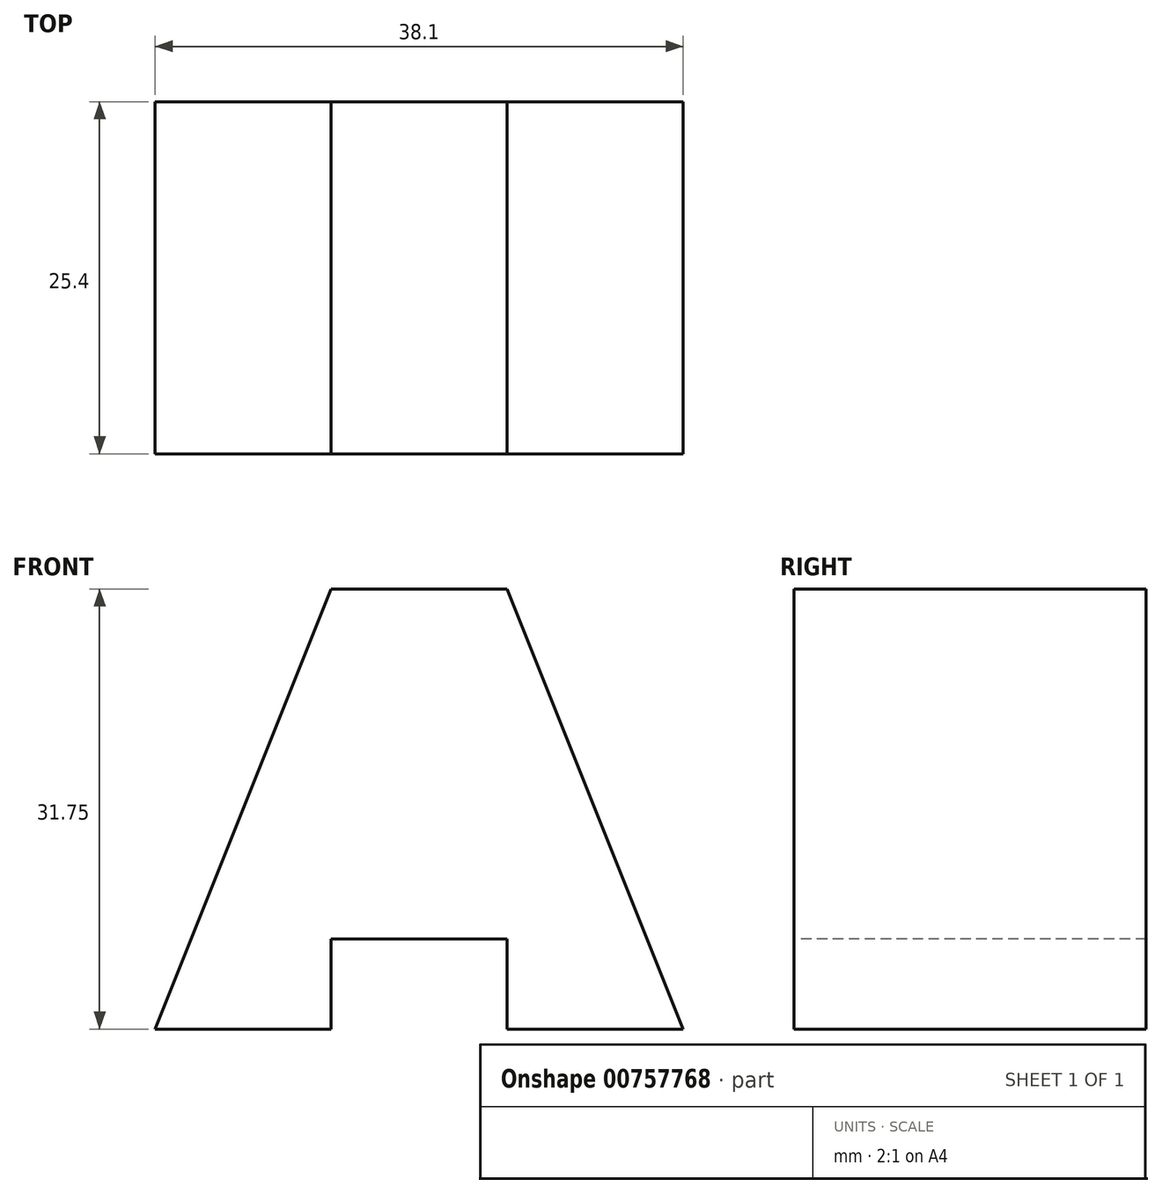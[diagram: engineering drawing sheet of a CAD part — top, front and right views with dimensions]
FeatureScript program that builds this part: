
annotation { "Feature Type Name" : "Feature", "Feature Type Description" : "" }
export const myFeature = defineFeature(function(context is Context, id is Id, definition is map)
    precondition{}
    {
        {
            var Q0;
            Q0=qCreatedBy(makeId("Right.planeOp"),FACE);
            var sketch = newSketch(context, id + "F0", { "sketchPlane" : qUnion([Q0])});
            skLineSegment(sketch, "E0", {"start": v(-12.7, 0) * mm, "end": v(0, 0) * mm});
            skLineSegment(sketch, "E1", {"start": v(0, 0) * mm, "end": v(12.7, 0) * mm});
            skLineSegment(sketch, "E2", {"start": v(12.7, 0) * mm, "end": v(12.7, 31.75) * mm});
            skLineSegment(sketch, "E3", {"start": v(12.7, 31.75) * mm, "end": v(-12.7, 31.75) * mm});
            skLineSegment(sketch, "E4", {"start": v(-12.7, 31.75) * mm, "end": v(-12.7, 0) * mm});
            skSolve(sketch);
        }
        {
            var Q0;
            Q0 = qSketchRegion(id + "F0", true);
            extrude(context, id + "F1", {"entities" : qUnion([Q0]), "depth" : 38.1 * mm, "offsetDistance" : 25.4 * mm});
        }
        {
            var Q0;
            Q0=makeQuery(id+"F1.opExtrude","SWEPT_FACE",FACE,{"disambiguationData":[OSD([sQuery(id+"F0.wireOp",EDGE,"E4")])]});
            var sketch = newSketch(context, id + "F2", { "sketchPlane" : qUnion([Q0])});
            skLineSegment(sketch, "E5", {"start": v(38.1, 0) * mm, "end": v(25.4, 31.75) * mm});
            skLineSegment(sketch, "E6", {"start": v(25.4, 31.75) * mm, "end": v(12.7, 31.75) * mm});
            skLineSegment(sketch, "E7", {"start": v(12.7, 31.75) * mm, "end": v(0, 0) * mm});
            skLineSegment(sketch, "E8", {"start": v(0, 0) * mm, "end": v(38.1, 0) * mm});
            skSolve(sketch);
        }
        {
            var Q0;
            {var subQ0=sQuery(id+"F2.wireOp",EDGE,"E7");Q0=makeQuery(id+"F2.imprint","IMPRINT",FACE,{"disambiguationData":[TD([[makeQuery(id+"F2.imprint","IMPRINT",EDGE,{"derivedFrom":subQ0}),-1.0]])]});}
            var Q1;
            {var subQ0=sQuery(id+"F2.wireOp",EDGE,"E5");Q1=makeQuery(id+"F2.imprint","IMPRINT",FACE,{"disambiguationData":[TD([[makeQuery(id+"F2.imprint","IMPRINT",EDGE,{"derivedFrom":subQ0}),-1.0]])]});}
            extrude(context, id + "F3", {"entities" : qUnion([Q0, Q1]), "operationType" : NewBodyOperationType.REMOVE, "endBound" : BoundingType.THROUGH_ALL, "oppositeDirection" : true, "depth" : 25.4 * mm, "offsetDistance" : 25.4 * mm});
        }
        {
            var Q0;
            Q0=makeQuery(id+"F1.opExtrude","SWEPT_FACE",FACE,{"disambiguationData":[OSD([sQuery(id+"F0.wireOp",EDGE,"E4")])]});
            var sketch = newSketch(context, id + "F4", { "sketchPlane" : qUnion([Q0])});
            skLineSegment(sketch, "E9", {"start": v(12.7, 0) * mm, "end": v(12.7, 6.49) * mm});
            skLineSegment(sketch, "E10", {"start": v(12.7, 6.49) * mm, "end": v(25.4, 6.49) * mm});
            skLineSegment(sketch, "E11", {"start": v(25.4, 6.49) * mm, "end": v(25.4, 0) * mm});
            skSolve(sketch);
        }
        {
            var Q0;
            Q0 = qSketchRegion(id + "F4", true);
            var Q1;
            {var subQ0=sQuery(id+"F4.wireOp",EDGE,"E9");Q1=makeQuery(id+"F4.imprint","IMPRINT",FACE,{"disambiguationData":[TD([[makeQuery(id+"F4.imprint","IMPRINT",EDGE,{"derivedFrom":subQ0}),-1.0]])]});}
            extrude(context, id + "F5", {"entities" : qUnion([Q0, Q1]), "operationType" : NewBodyOperationType.REMOVE, "endBound" : BoundingType.THROUGH_ALL, "oppositeDirection" : true, "depth" : 25.4 * mm, "offsetDistance" : 25.4 * mm});
        }
    });
